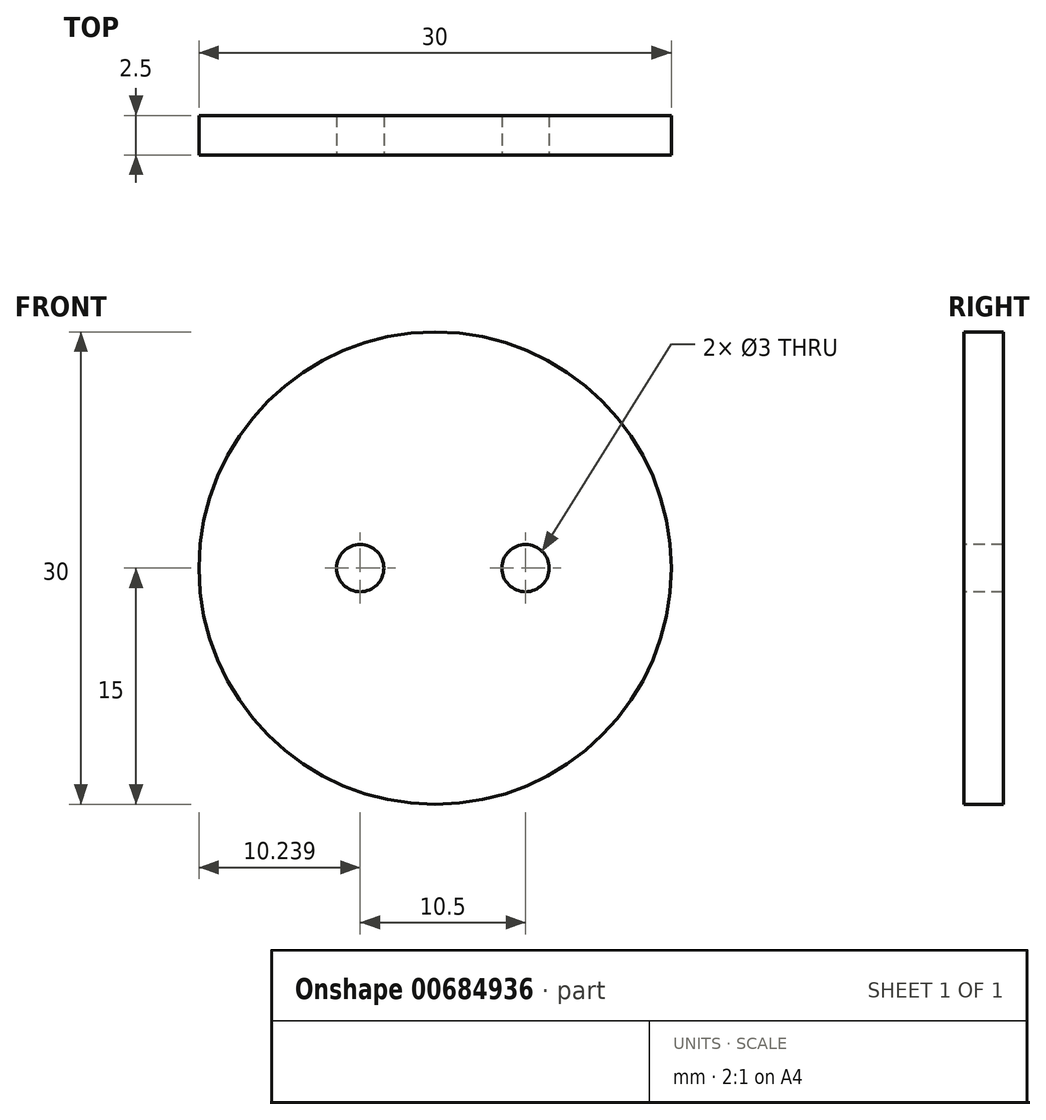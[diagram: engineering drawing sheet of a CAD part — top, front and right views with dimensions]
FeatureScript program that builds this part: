
annotation { "Feature Type Name" : "Feature", "Feature Type Description" : "" }
export const myFeature = defineFeature(function(context is Context, id is Id, definition is map)
    precondition{}
    {
        {
            var Q0;
            Q0=qCreatedBy(makeId("Front.planeOp"),FACE);
            var sketch = newSketch(context, id + "F0", { "sketchPlane" : qUnion([Q0])});
            skCircle(sketch, "E0", {"center": v(0, 0) * mm, "radius": 15 * mm});
            skSolve(sketch);
        }
        {
            var Q0;
            Q0=makeQuery(id+"F0.imprint","IMPRINT",FACE,{"disambiguationData":[TD([[makeQuery(id+"F0.imprint","IMPRINT",EDGE,{"derivedFrom":sQuery(id+"F0.wireOp",EDGE,"E0")}),1.0]])]});
            extrude(context, id + "F1", {"entities" : qUnion([Q0]), "depth" : 2.5 * mm, "offsetDistance" : 25 * mm});
        }
        {
            var Q0;
            Q0=makeQuery(id+"F1.opExtrude","CAP_FACE",FACE,{"disambiguationData":[OSD([sQuery(id+"F0.wireOp",EDGE,"E0")])],"isStart":false});
            var sketch = newSketch(context, id + "F2", { "sketchPlane" : qUnion([Q0])});
            skCircle(sketch, "E1", {"center": v(-4.76, 0) * mm, "radius": 1.5 * mm});
            skCircle(sketch, "E2", {"center": v(5.74, 0) * mm, "radius": 1.5 * mm});
            skSolve(sketch);
        }
        {
            var Q0;
            Q0=makeQuery(id+"F2.imprint","IMPRINT",FACE,{"disambiguationData":[TD([[makeQuery(id+"F2.imprint","IMPRINT",EDGE,{"derivedFrom":sQuery(id+"F2.wireOp",EDGE,"E1")}),1.0]])]});
            var Q1;
            Q1=makeQuery(id+"F2.imprint","IMPRINT",FACE,{"disambiguationData":[TD([[makeQuery(id+"F2.imprint","IMPRINT",EDGE,{"derivedFrom":sQuery(id+"F2.wireOp",EDGE,"E2")}),1.0]])]});
            extrude(context, id + "F3", {"entities" : qUnion([Q0, Q1]), "operationType" : NewBodyOperationType.REMOVE, "oppositeDirection" : true, "depth" : 5 * mm, "offsetDistance" : 25 * mm});
        }
    });
